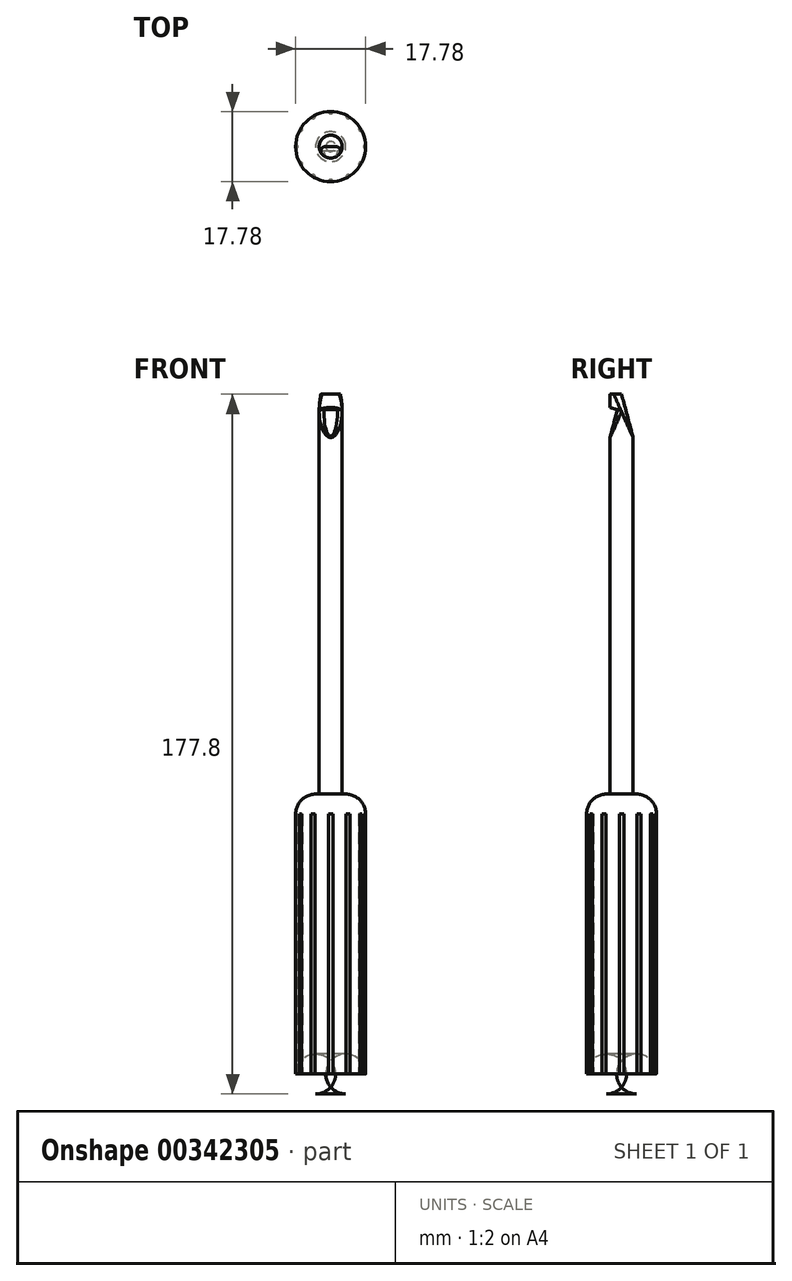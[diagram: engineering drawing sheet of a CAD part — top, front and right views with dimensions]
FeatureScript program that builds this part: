
annotation { "Feature Type Name" : "Feature", "Feature Type Description" : "" }
export const myFeature = defineFeature(function(context is Context, id is Id, definition is map)
    precondition{}
    {
        {
            var Q0;
            Q0=qCreatedBy(makeId("Top.planeOp"),FACE);
            var sketch = newSketch(context, id + "F0", { "sketchPlane" : qUnion([Q0])});
            skCircle(sketch, "E0", {"center": v(0, 0) * mm, "radius": 8.9 * mm});
            skSolve(sketch);
        }
        {
            var Q0;
            Q0=makeQuery(id+"F0.imprint","IMPRINT",FACE,{"disambiguationData":[TD([[makeQuery(id+"F0.imprint","IMPRINT",EDGE,{"derivedFrom":sQuery(id+"F0.wireOp",EDGE,"E0")}),1.0]])]});
            extrude(context, id + "F1", {"entities" : qUnion([Q0]), "endBound" : BoundingType.SYMMETRIC, "depth" : 76.2 * mm});
        }
        {
            var Q0;
            Q0=makeQuery(id+"F1.opExtrude","CAP_EDGE",EDGE,{"disambiguationData":[OSD([sQuery(id+"F0.wireOp",EDGE,"E0")])],"isStart":true});
            var Q1;
            Q1=makeQuery(id+"F1.opExtrude","CAP_EDGE",EDGE,{"disambiguationData":[OSD([sQuery(id+"F0.wireOp",EDGE,"E0")])],"isStart":false});
            fillet(context, id + "F2", {"entities" : qUnion([Q0, Q1]), "radius" : 5.08 * mm, "tangentPropagation" : true, "allowEdgeOverflow" : false});
        }
        {
            var Q0;
            Q0=makeQuery(id+"F1.opExtrude","CAP_FACE",FACE,{"disambiguationData":[OSD([sQuery(id+"F0.wireOp",EDGE,"E0")])],"isStart":false});
            var sketch = newSketch(context, id + "F3", { "sketchPlane" : qUnion([Q0])});
            skCircle(sketch, "E1", {"center": v(0, 0) * mm, "radius": 2.92 * mm});
            skSolve(sketch);
        }
        {
            var Q0;
            Q0=makeQuery(id+"F3.imprint","IMPRINT",FACE,{"disambiguationData":[TD([[makeQuery(id+"F3.imprint","IMPRINT",EDGE,{"derivedFrom":sQuery(id+"F3.wireOp",EDGE,"E1")}),1.0]])]});
            extrude(context, id + "F4", {"entities" : qUnion([Q0]), "operationType" : NewBodyOperationType.ADD, "depth" : 101.6 * mm});
        }
        {
            var Q0;
            Q0=makeQuery(id+"F4.opExtrude","CAP_FACE",FACE,{"disambiguationData":[OSD([sQuery(id+"F3.wireOp",EDGE,"E1")])],"isStart":false});
            var sketch = newSketch(context, id + "F5", { "sketchPlane" : qUnion([Q0])});
            skLineSegment(sketch, "E2", {"start": v(-2.92, 0) * mm, "end": v(2.92, 0) * mm, "construction": true});
            skSolve(sketch);
        }
        {
            var Q0;
            Q0=sQuery(id+"F5.wireOp",EDGE,"E2");
            cPlane(context, id + "F6", {"entities" : qUnion([Q0]), "cplaneType" : CPlaneType.LINE_ANGLE, "offset" : 25.4 * mm, "angle" : 15 * degree, "width" : 152.4 * mm, "height" : 152.4 * mm});
        }
        {
            var Q0;
            Q0=qCreatedBy(id+"F6.planeOp",FACE);
            var sketch = newSketch(context, id + "F7", { "sketchPlane" : qUnion([Q0])});
            skLineSegment(sketch, "E3.bottom", {"start": v(-10.7, 99.95) * mm, "end": v(15.02, 99.95) * mm});
            skLineSegment(sketch, "E3.top", {"start": v(-10.7, 138.62) * mm, "end": v(15.02, 138.62) * mm});
            skLineSegment(sketch, "E3.left", {"start": v(-10.7, 99.95) * mm, "end": v(-10.7, 138.62) * mm});
            skLineSegment(sketch, "E3.right", {"start": v(15.02, 99.95) * mm, "end": v(15.02, 138.62) * mm});
            skSolve(sketch);
        }
        {
            var Q0;
            Q0=makeQuery(id+"F7.imprint","IMPRINT",FACE,{"disambiguationData":[TD([[makeQuery(id+"F7.imprint","IMPRINT",EDGE,{"derivedFrom":sQuery(id+"F7.wireOp",EDGE,"E3.bottom")}),1.0]])]});
            extrude(context, id + "F8", {"entities" : qUnion([Q0]), "operationType" : NewBodyOperationType.REMOVE, "depth" : 6.35 * mm});
        }
        {
            var Q0;
            Q0=makeQuery(id+"F8.boolean.opBoolean","INTERSECT",EDGE,{"derivedFrom":[makeQuery(id+"F4.opExtrude","CAP_FACE",FACE,{"disambiguationData":[OSD([sQuery(id+"F3.wireOp",EDGE,"E1")])],"isStart":false}),makeQuery(id+"F8.opExtrude","CAP_FACE",FACE,{"disambiguationData":[OSD([sQuery(id+"F7.wireOp",EDGE,"E3.bottom"),sQuery(id+"F7.wireOp",EDGE,"E3.top"),sQuery(id+"F7.wireOp",EDGE,"E3.left"),sQuery(id+"F7.wireOp",EDGE,"E3.right")])],"isStart":true})]});
            cPlane(context, id + "F9", {"entities" : qUnion([Q0]), "cplaneType" : CPlaneType.LINE_ANGLE, "offset" : 25.4 * mm, "angle" : 15 * degree, "width" : 152.4 * mm, "height" : 152.4 * mm});
        }
        {
            var Q0;
            Q0=qCreatedBy(id+"F9.planeOp",FACE);
            var sketch = newSketch(context, id + "F10", { "sketchPlane" : qUnion([Q0])});
            skLineSegment(sketch, "E4.bottom", {"start": v(-8.52, 130.89) * mm, "end": v(12.01, 130.89) * mm});
            skLineSegment(sketch, "E4.top", {"start": v(-8.52, 102.68) * mm, "end": v(12.01, 102.68) * mm});
            skLineSegment(sketch, "E4.left", {"start": v(-8.52, 130.89) * mm, "end": v(-8.52, 102.68) * mm});
            skLineSegment(sketch, "E4.right", {"start": v(12.01, 130.89) * mm, "end": v(12.01, 102.68) * mm});
            skLineSegment(sketch, "E5.bottom", {"start": v(12.01, 130.89) * mm, "end": v(-8.52, 130.89) * mm});
            skLineSegment(sketch, "E5.top", {"start": v(12.01, 138.82) * mm, "end": v(-8.52, 138.82) * mm});
            skLineSegment(sketch, "E5.left", {"start": v(12.01, 130.89) * mm, "end": v(12.01, 138.82) * mm});
            skLineSegment(sketch, "E5.right", {"start": v(-8.52, 130.89) * mm, "end": v(-8.52, 138.82) * mm});
            skSolve(sketch);
        }
        {
            var Q0;
            Q0=makeQuery(id+"F10.imprint","IMPRINT",FACE,{"disambiguationData":[TD([[makeQuery(id+"F10.imprint","IMPRINT",EDGE,{"derivedFrom":sQuery(id+"F10.wireOp",EDGE,"E4.bottom")}),-1.0]])]});
            var Q1;
            Q1=makeQuery(id+"F10.imprint","IMPRINT",FACE,{"disambiguationData":[TD([[makeQuery(id+"F10.imprint","IMPRINT",EDGE,{"derivedFrom":sQuery(id+"F10.wireOp",EDGE,"E5.bottom")}),-1.0]])]});
            var Q2;
            Q2=makeQuery(id+"F10.imprint","IMPRINT",FACE,{"disambiguationData":[TD([[makeQuery(id+"F10.imprint","IMPRINT",EDGE,{"derivedFrom":sQuery(id+"F10.wireOp",EDGE,"E4.top")}),1.0]])]});
            extrude(context, id + "F11", {"entities" : qUnion([Q0, Q1, Q2]), "operationType" : NewBodyOperationType.REMOVE, "depth" : 39.12 * mm});
        }
        {
            var Q0;
            Q0=makeQuery(id+"F11.boolean.opBoolean","INTERSECT",EDGE,{"derivedFrom":[makeQuery(id+"F4.opExtrude","SWEPT_FACE",FACE,{"disambiguationData":[OSD([sQuery(id+"F3.wireOp",EDGE,"E1")])]}),makeQuery(id+"F11.opExtrude","CAP_FACE",FACE,{"disambiguationData":[OSD([sQuery(id+"F10.wireOp",EDGE,"E4.bottom"),sQuery(id+"F10.wireOp",EDGE,"E4.top"),sQuery(id+"F10.wireOp",EDGE,"E4.left"),sQuery(id+"F10.wireOp",EDGE,"E4.right")])],"isStart":true})]});
            var Q1;
            Q1=makeQuery(id+"F8.boolean.opBoolean","INTERSECT",EDGE,{"derivedFrom":[makeQuery(id+"F4.opExtrude","SWEPT_FACE",FACE,{"disambiguationData":[OSD([sQuery(id+"F3.wireOp",EDGE,"E1")])]}),makeQuery(id+"F8.opExtrude","CAP_FACE",FACE,{"disambiguationData":[OSD([sQuery(id+"F7.wireOp",EDGE,"E3.bottom"),sQuery(id+"F7.wireOp",EDGE,"E3.top"),sQuery(id+"F7.wireOp",EDGE,"E3.left"),sQuery(id+"F7.wireOp",EDGE,"E3.right")])],"isStart":true})]});
            fillet(context, id + "F12", {"entities" : qUnion([Q0, Q1]), "radius" : 1.16 * mm, "tangentPropagation" : true, "allowEdgeOverflow" : false});
        }
        {
            var Q0;
            Q0=qCreatedBy(makeId("Top.planeOp"),FACE);
            var sketch = newSketch(context, id + "F13", { "sketchPlane" : qUnion([Q0])});
            skPoint(sketch, "E6.center.orphan", {"position": v(-7.04, 0) * mm});
            skCircle(sketch, "E7", {"center": v(-8.9, 0) * mm, "radius": 0.57 * mm});
            skSolve(sketch);
        }
        {
            var Q0;
            Q0=makeQuery(id+"F13.imprint","IMPRINT",FACE,{"disambiguationData":[TD([[makeQuery(id+"F13.imprint","IMPRINT",EDGE,{"derivedFrom":sQuery(id+"F13.wireOp",EDGE,"E7")}),1.0]])]});
            extrude(context, id + "F14", {"entities" : qUnion([Q0]), "endBound" : BoundingType.SYMMETRIC, "depth" : 65.99 * mm});
        }
        {
            var Q0;
            Q0=qCreatedBy(makeId("Right.planeOp"),FACE);
            var sketch = newSketch(context, id + "F15", { "sketchPlane" : qUnion([Q0])});
            skLineSegment(sketch, "E8", {"start": v(0, 69.6) * mm, "end": v(0, -41.5) * mm});
            skLineSegment(sketch, "E9", {"start": v(0, 69.6) * mm, "end": v(0, 157.36) * mm, "construction": true});
            skSolve(sketch);
        }
        {
            var Q0;
            Q0=makeQuery(id+"F14.opExtrude","SWEPT_BODY",BODY,{"disambiguationData":[OSD([sQuery(id+"F13.wireOp",EDGE,"E7")])]});
            var Q1;
            Q1=sQuery(id+"F15.wireOp",EDGE,"E9");
            circularPattern(context, id + "F16", {"operationType" : NewBodyOperationType.REMOVE, "entities" : qUnion([Q0]), "axis" : qUnion([Q1]), "angle" : 360 * degree, "instanceCount" : 12, "equalSpace" : true});
        }
    });
